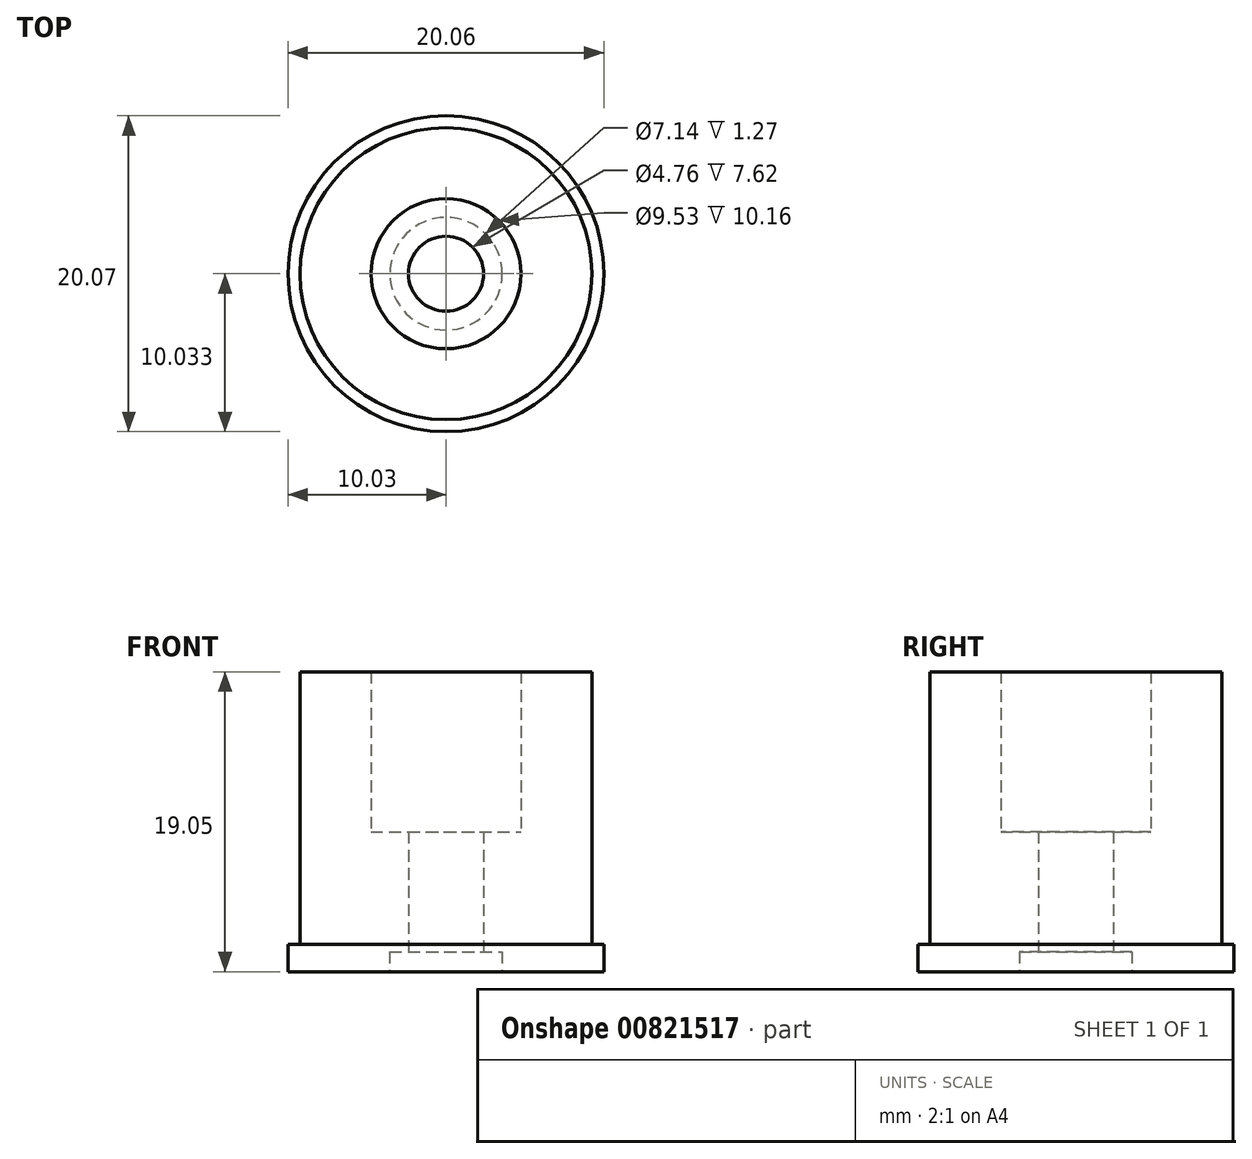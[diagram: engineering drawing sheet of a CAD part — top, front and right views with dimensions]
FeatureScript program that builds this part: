
annotation { "Feature Type Name" : "Feature", "Feature Type Description" : "" }
export const myFeature = defineFeature(function(context is Context, id is Id, definition is map)
    precondition{}
    {
        {
            var Q0;
            Q0=qCreatedBy(makeId("Right.planeOp"),FACE);
            var sketch = newSketch(context, id + "F0", { "sketchPlane" : qUnion([Q0])});
            skLineSegment(sketch, "E0", {"start": v(0, 0) * mm, "end": v(0, 1.73) * mm});
            skLineSegment(sketch, "E1", {"start": v(0, 1.73) * mm, "end": v(0.76, 1.73) * mm});
            skLineSegment(sketch, "E2", {"start": v(10.03, 0) * mm, "end": v(10.03, 19.05) * mm});
            skLineSegment(sketch, "E3", {"start": v(0.76, 1.73) * mm, "end": v(0.76, 19.05) * mm});
            skLineSegment(sketch, "E4", {"start": v(5.27, 19.05) * mm, "end": v(0.76, 19.05) * mm});
            skLineSegment(sketch, "E5", {"start": v(5.27, 19.05) * mm, "end": v(5.27, 8.89) * mm});
            skLineSegment(sketch, "E6", {"start": v(5.27, 8.89) * mm, "end": v(7.65, 8.89) * mm});
            skLineSegment(sketch, "E7", {"start": v(5.27, 8.89) * mm, "end": v(5.27, 19.05) * mm});
            skLineSegment(sketch, "E8", {"start": v(6.46, 0) * mm, "end": v(6.46, 1.27) * mm});
            skLineSegment(sketch, "E9", {"start": v(7.65, 8.89) * mm, "end": v(7.65, 1.27) * mm});
            skLineSegment(sketch, "E10", {"start": v(6.46, 0) * mm, "end": v(0, 0) * mm});
            skLineSegment(sketch, "E11", {"start": v(7.65, 1.27) * mm, "end": v(6.46, 1.27) * mm});
            skSolve(sketch);
        }
        {
            var Q0;
            Q0=makeQuery(id+"F0.imprint","IMPRINT",FACE,{"disambiguationData":[TD([[makeQuery(id+"F0.imprint","IMPRINT",EDGE,{"derivedFrom":sQuery(id+"F0.wireOp",EDGE,"E0")}),-1.0]])]});
            var Q1;
            Q1=sQuery(id+"F0.wireOp",EDGE,"E2");
            revolve(context, id + "F1", {"surfaceOperationType" : NewSurfaceOperationType.NEW, "entities" : qUnion([Q0]), "axis" : qUnion([Q1]), "revolveType" : RevolveType.FULL});
        }
    });
